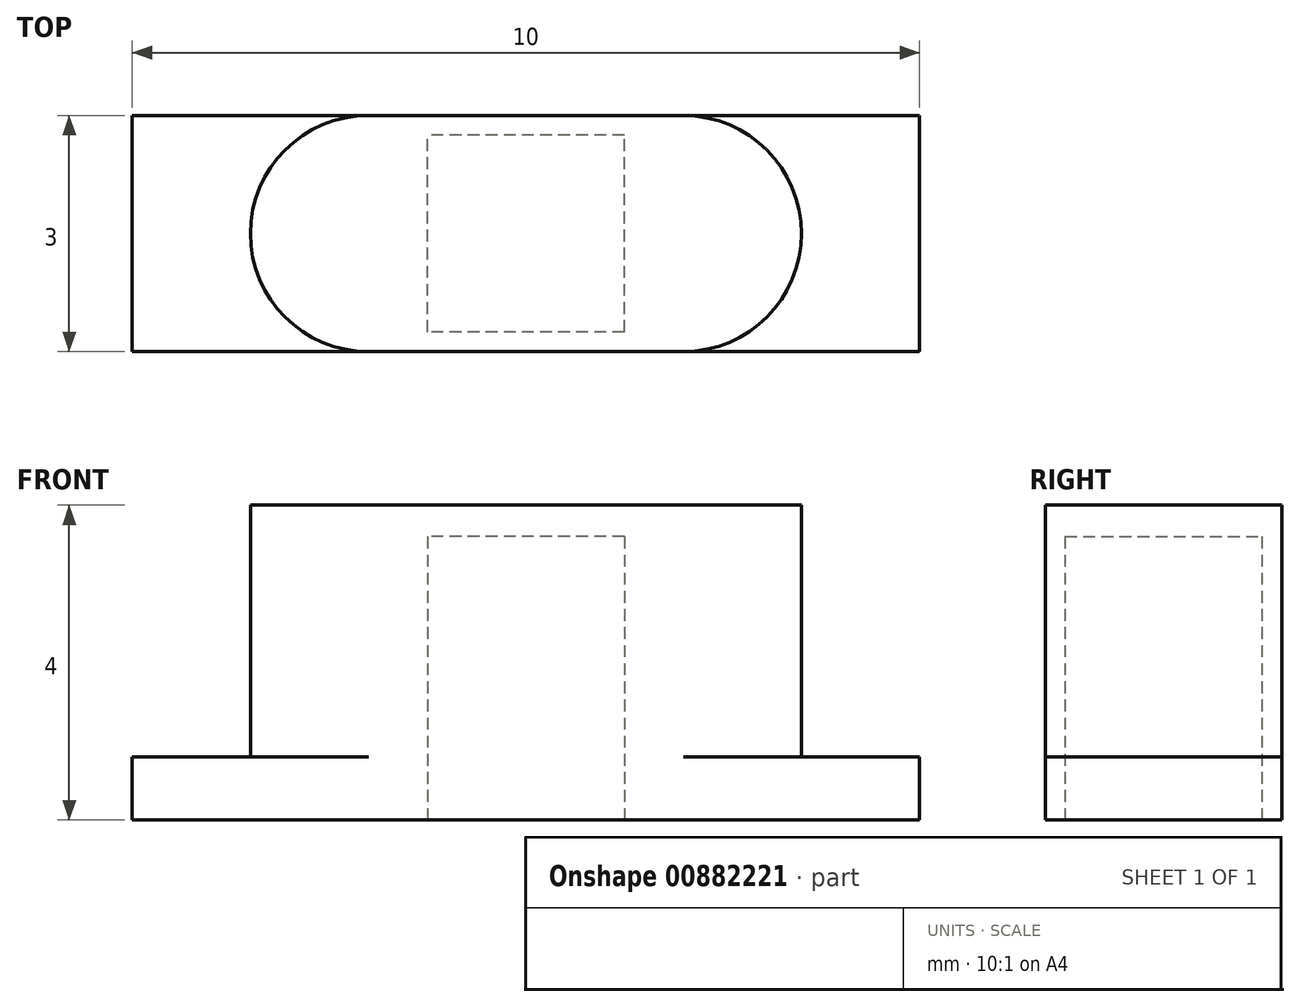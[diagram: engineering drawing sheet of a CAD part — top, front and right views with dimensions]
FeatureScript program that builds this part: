
annotation { "Feature Type Name" : "Feature", "Feature Type Description" : "" }
export const myFeature = defineFeature(function(context is Context, id is Id, definition is map)
    precondition{}
    {
        {
            var Q0;
            Q0=qCreatedBy(makeId("Top.planeOp"),FACE);
            var sketch = newSketch(context, id + "F0", { "sketchPlane" : qUnion([Q0])});
            skLineSegment(sketch, "E0.bottom", {"start": v(3.5, 1.5) * mm, "end": v(-3.5, 1.5) * mm});
            skLineSegment(sketch, "E0.top", {"start": v(3.5, -1.5) * mm, "end": v(-3.5, -1.5) * mm});
            skLineSegment(sketch, "E0.left", {"start": v(3.5, 1.5) * mm, "end": v(3.5, -1.5) * mm});
            skLineSegment(sketch, "E0.right", {"start": v(-3.5, 1.5) * mm, "end": v(-3.5, -1.5) * mm});
            skPoint(sketch, "E0.middle", {"position": v(0, 0) * mm});
            skLineSegment(sketch, "E1.bottom", {"start": v(-5, 1.5) * mm, "end": v(5, 1.5) * mm});
            skLineSegment(sketch, "E1.top", {"start": v(-5, -1.5) * mm, "end": v(5, -1.5) * mm});
            skLineSegment(sketch, "E1.left", {"start": v(-5, 1.5) * mm, "end": v(-5, -1.5) * mm});
            skLineSegment(sketch, "E1.right", {"start": v(5, 1.5) * mm, "end": v(5, -1.5) * mm});
            skLineSegment(sketch, "E2.bottom", {"start": v(1.25, -1.25) * mm, "end": v(-1.25, -1.25) * mm});
            skLineSegment(sketch, "E2.top", {"start": v(1.25, 1.25) * mm, "end": v(-1.25, 1.25) * mm});
            skLineSegment(sketch, "E2.left", {"start": v(1.25, -1.25) * mm, "end": v(1.25, 1.25) * mm});
            skLineSegment(sketch, "E2.right", {"start": v(-1.25, -1.25) * mm, "end": v(-1.25, 1.25) * mm});
            skSolve(sketch);
        }
        {
            var Q0;
            {var subQ0=sQuery(id+"F0.wireOp",EDGE,"E0.left");Q0=makeQuery(id+"F0.imprint","IMPRINT",FACE,{"disambiguationData":[TD([[makeQuery(id+"F0.imprint","IMPRINT",EDGE,{"derivedFrom":subQ0}),-1.0]])]});}
            var Q1;
            Q1=makeQuery(id+"F0.imprint","IMPRINT",FACE,{"disambiguationData":[TD([[makeQuery(id+"F0.imprint","IMPRINT",EDGE,{"derivedFrom":sQuery(id+"F0.wireOp",EDGE,"E2.bottom")}),-1.0]])]});
            extrude(context, id + "F1", {"entities" : qUnion([Q0, Q1]), "depth" : 4 * mm, "offsetDistance" : 25 * mm});
        }
        {
            var Q0;
            {var subQ0=sQuery(id+"F0.wireOp",EDGE,"E0.right");Q0=makeQuery(id+"F0.imprint","IMPRINT",FACE,{"disambiguationData":[TD([[makeQuery(id+"F0.imprint","IMPRINT",EDGE,{"derivedFrom":subQ0}),-1.0]])]});}
            var Q1;
            {var subQ0=sQuery(id+"F0.wireOp",EDGE,"E0.left");Q1=makeQuery(id+"F0.imprint","IMPRINT",FACE,{"disambiguationData":[TD([[makeQuery(id+"F0.imprint","IMPRINT",EDGE,{"derivedFrom":subQ0}),1.0]])]});}
            extrude(context, id + "F2", {"entities" : qUnion([Q0, Q1]), "operationType" : NewBodyOperationType.ADD, "depth" : 0.8 * mm, "offsetDistance" : 25 * mm});
        }
        {
            var Q0;
            Q0=makeQuery(id+"F1.opExtrude","SWEPT_EDGE",EDGE,{"disambiguationData":[OSD([sQuery(id+"F0.wireOp",EDGE,"E0.right"),sQuery(id+"F0.wireOp",EDGE,"E1.bottom")])]});
            var Q1;
            Q1=makeQuery(id+"F1.opExtrude","SWEPT_EDGE",EDGE,{"disambiguationData":[OSD([sQuery(id+"F0.wireOp",EDGE,"E0.right"),sQuery(id+"F0.wireOp",EDGE,"E1.top")])]});
            var Q2;
            Q2=makeQuery(id+"F1.opExtrude","SWEPT_EDGE",EDGE,{"disambiguationData":[OSD([sQuery(id+"F0.wireOp",EDGE,"E0.left"),sQuery(id+"F0.wireOp",EDGE,"E1.top")])]});
            var Q3;
            Q3=makeQuery(id+"F1.opExtrude","SWEPT_EDGE",EDGE,{"disambiguationData":[OSD([sQuery(id+"F0.wireOp",EDGE,"E0.left"),sQuery(id+"F0.wireOp",EDGE,"E1.bottom")])]});
            fillet(context, id + "F3", {"entities" : qUnion([Q0, Q1, Q2, Q3]), "radius" : 1.5 * mm, "tangentPropagation" : true, "allowEdgeOverflow" : false});
        }
        {
            var Q0;
            Q0=makeQuery(id+"F0.imprint","IMPRINT",FACE,{"disambiguationData":[TD([[makeQuery(id+"F0.imprint","IMPRINT",EDGE,{"derivedFrom":sQuery(id+"F0.wireOp",EDGE,"E2.bottom")}),-1.0]])]});
            extrude(context, id + "F4", {"entities" : qUnion([Q0]), "operationType" : NewBodyOperationType.REMOVE, "depth" : 3.6 * mm, "offsetDistance" : 25 * mm});
        }
    });
